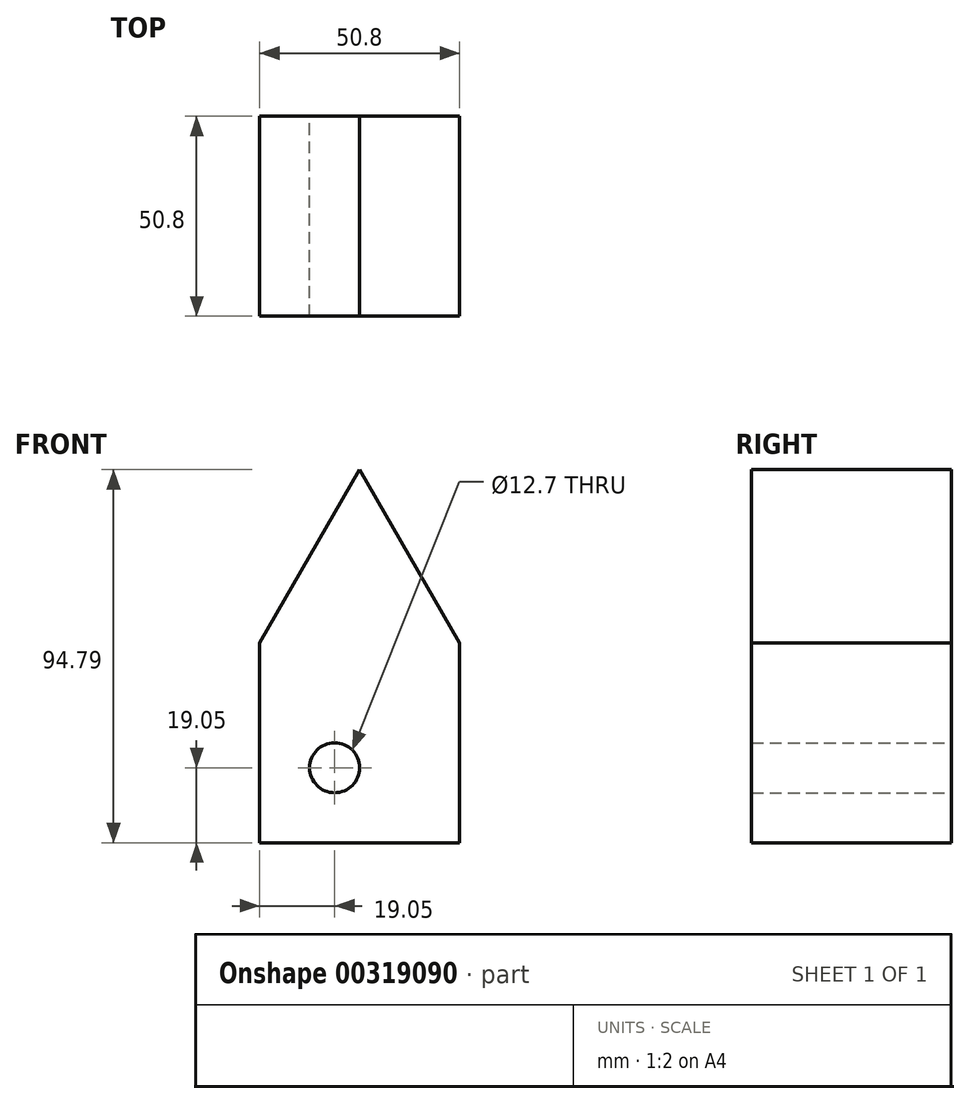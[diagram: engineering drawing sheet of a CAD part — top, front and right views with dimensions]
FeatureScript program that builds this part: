
annotation { "Feature Type Name" : "Feature", "Feature Type Description" : "" }
export const myFeature = defineFeature(function(context is Context, id is Id, definition is map)
    precondition{}
    {
        {
            var Q0;
            Q0=qCreatedBy(makeId("Front.planeOp"),FACE);
            var sketch = newSketch(context, id + "F0", { "sketchPlane" : qUnion([Q0])});
            skLineSegment(sketch, "E0.top", {"start": v(25.4, -25.4) * mm, "end": v(-25.4, -25.4) * mm});
            skLineSegment(sketch, "E0.left", {"start": v(25.4, 25.4) * mm, "end": v(25.4, -25.4) * mm});
            skLineSegment(sketch, "E0.right", {"start": v(-25.4, 25.4) * mm, "end": v(-25.4, -25.4) * mm});
            skPoint(sketch, "E0.middle", {"position": v(0, 0) * mm});
            skLineSegment(sketch, "E1", {"start": v(-25.4, 25.4) * mm, "end": v(0, 69.4) * mm});
            skLineSegment(sketch, "E2", {"start": v(25.4, 25.4) * mm, "end": v(0, 69.4) * mm});
            skCircle(sketch, "E3", {"center": v(-6.35, -6.35) * mm, "radius": 6.35 * mm});
            skSolve(sketch);
        }
        {
            var Q0;
            Q0=makeQuery(id+"F0.imprint","IMPRINT",FACE,{"disambiguationData":[TD([[makeQuery(id+"F0.imprint","IMPRINT",EDGE,{"derivedFrom":sQuery(id+"F0.wireOp",EDGE,"E0.top")}),-1.0]])]});
            extrude(context, id + "F1", {"entities" : qUnion([Q0]), "depth" : 50.8 * mm});
        }
    });
